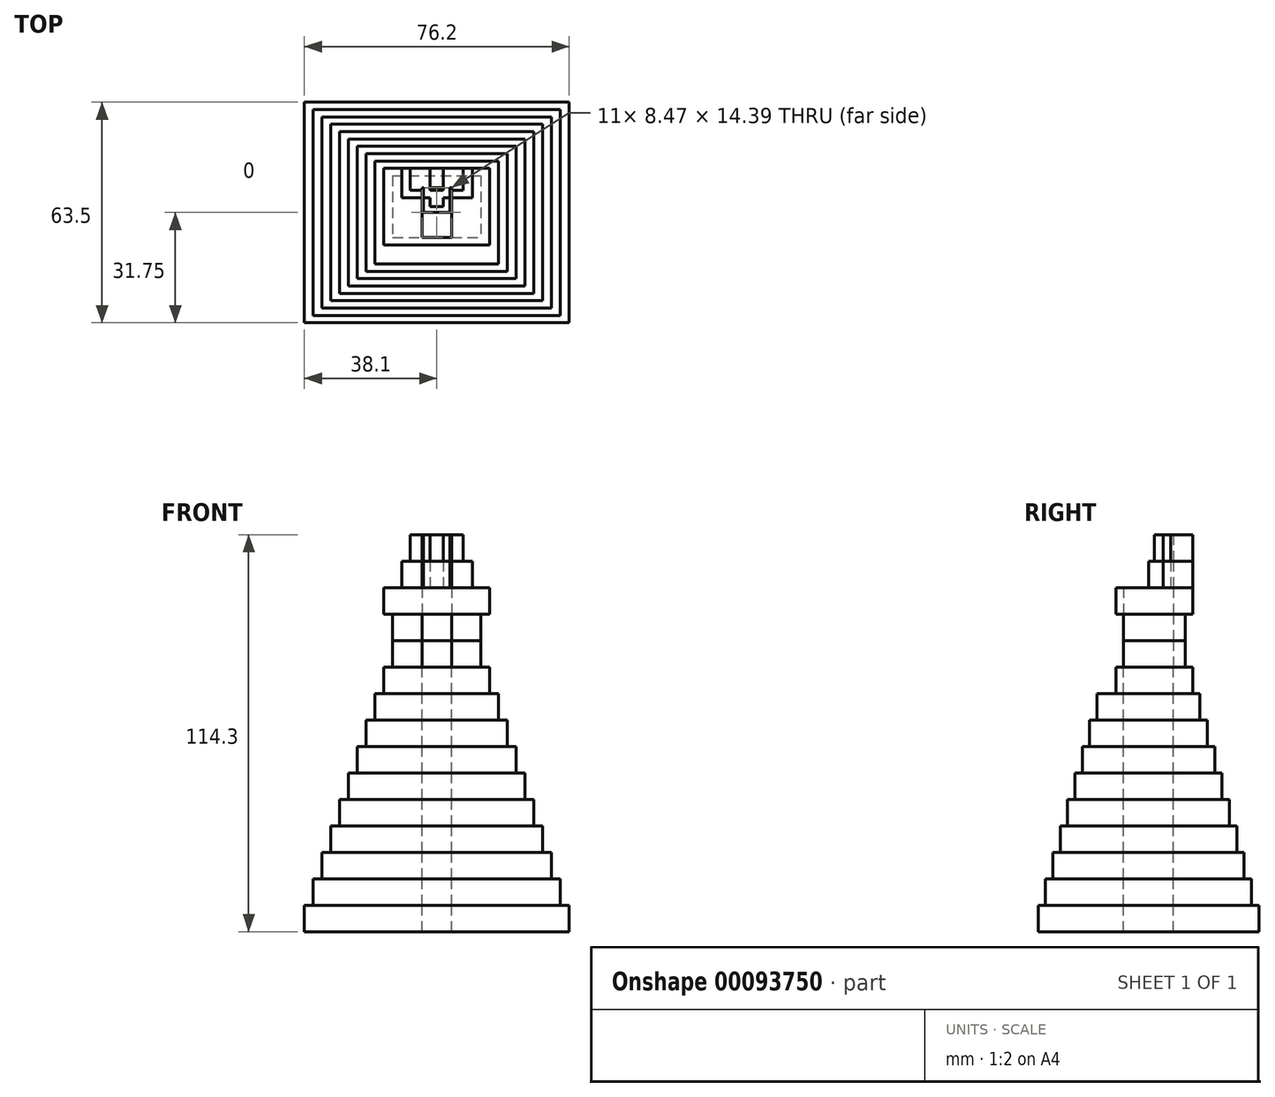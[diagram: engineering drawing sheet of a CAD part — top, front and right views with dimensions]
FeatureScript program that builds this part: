
annotation { "Feature Type Name" : "Feature", "Feature Type Description" : "" }
export const myFeature = defineFeature(function(context is Context, id is Id, definition is map)
    precondition{}
    {
        {
            var Q0;
            Q0=qCreatedBy(makeId("Top.planeOp"),FACE);
            var sketch = newSketch(context, id + "F0", { "sketchPlane" : qUnion([Q0])});
            skLineSegment(sketch, "E0.bottom", {"start": v(-38.1, 31.75) * mm, "end": v(38.1, 31.75) * mm});
            skLineSegment(sketch, "E0.top", {"start": v(-38.1, -31.75) * mm, "end": v(38.1, -31.75) * mm});
            skLineSegment(sketch, "E0.left", {"start": v(-38.1, 31.75) * mm, "end": v(-38.1, -31.75) * mm});
            skLineSegment(sketch, "E0.right", {"start": v(38.1, 31.75) * mm, "end": v(38.1, -31.75) * mm});
            skPoint(sketch, "E0.middle", {"position": v(0, 0) * mm});
            skLineSegment(sketch, "E1.bottom", {"start": v(-35.56, 29.63) * mm, "end": v(35.56, 29.63) * mm});
            skLineSegment(sketch, "E1.top", {"start": v(-35.56, -29.63) * mm, "end": v(35.56, -29.63) * mm});
            skLineSegment(sketch, "E1.left", {"start": v(-35.56, 29.63) * mm, "end": v(-35.56, -29.63) * mm});
            skLineSegment(sketch, "E1.right", {"start": v(35.56, 29.63) * mm, "end": v(35.56, -29.63) * mm});
            skLineSegment(sketch, "E2.bottom", {"start": v(-33.02, 27.52) * mm, "end": v(33.02, 27.52) * mm});
            skLineSegment(sketch, "E2.top", {"start": v(-33.02, -27.52) * mm, "end": v(33.02, -27.52) * mm});
            skLineSegment(sketch, "E2.left", {"start": v(-33.02, 27.52) * mm, "end": v(-33.02, -27.52) * mm});
            skLineSegment(sketch, "E2.right", {"start": v(33.02, 27.52) * mm, "end": v(33.02, -27.52) * mm});
            skLineSegment(sketch, "E3.bottom", {"start": v(-27.94, 23.28) * mm, "end": v(27.94, 23.28) * mm});
            skLineSegment(sketch, "E3.top", {"start": v(-27.94, -23.28) * mm, "end": v(27.94, -23.28) * mm});
            skLineSegment(sketch, "E3.left", {"start": v(-27.94, 23.28) * mm, "end": v(-27.94, -23.28) * mm});
            skLineSegment(sketch, "E3.right", {"start": v(27.94, 23.28) * mm, "end": v(27.94, -23.28) * mm});
            skLineSegment(sketch, "E4.bottom", {"start": v(-30.48, 25.4) * mm, "end": v(30.48, 25.4) * mm});
            skLineSegment(sketch, "E4.top", {"start": v(-30.48, -25.4) * mm, "end": v(30.48, -25.4) * mm});
            skLineSegment(sketch, "E4.left", {"start": v(-30.48, 25.4) * mm, "end": v(-30.48, -25.4) * mm});
            skLineSegment(sketch, "E4.right", {"start": v(30.48, 25.4) * mm, "end": v(30.48, -25.4) * mm});
            skLineSegment(sketch, "E5.bottom", {"start": v(-25.4, 21.17) * mm, "end": v(25.4, 21.17) * mm});
            skLineSegment(sketch, "E5.top", {"start": v(-25.4, -21.17) * mm, "end": v(25.4, -21.17) * mm});
            skLineSegment(sketch, "E5.left", {"start": v(-25.4, 21.17) * mm, "end": v(-25.4, -21.17) * mm});
            skLineSegment(sketch, "E5.right", {"start": v(25.4, 21.17) * mm, "end": v(25.4, -21.17) * mm});
            skLineSegment(sketch, "E6.bottom", {"start": v(-22.86, 19.05) * mm, "end": v(22.86, 19.05) * mm});
            skLineSegment(sketch, "E6.top", {"start": v(-22.86, -19.05) * mm, "end": v(22.86, -19.05) * mm});
            skLineSegment(sketch, "E6.left", {"start": v(-22.86, 19.05) * mm, "end": v(-22.86, -19.05) * mm});
            skLineSegment(sketch, "E6.right", {"start": v(22.86, 19.05) * mm, "end": v(22.86, -19.05) * mm});
            skLineSegment(sketch, "E7.bottom", {"start": v(-20.32, 16.93) * mm, "end": v(20.32, 16.93) * mm});
            skLineSegment(sketch, "E7.top", {"start": v(-20.32, -16.93) * mm, "end": v(20.32, -16.93) * mm});
            skLineSegment(sketch, "E7.left", {"start": v(-20.32, 16.93) * mm, "end": v(-20.32, -16.93) * mm});
            skLineSegment(sketch, "E7.right", {"start": v(20.32, 16.93) * mm, "end": v(20.32, -16.93) * mm});
            skLineSegment(sketch, "E8.bottom", {"start": v(-17.78, 14.82) * mm, "end": v(17.78, 14.82) * mm});
            skLineSegment(sketch, "E8.top", {"start": v(-17.78, -14.82) * mm, "end": v(17.78, -14.82) * mm});
            skLineSegment(sketch, "E8.left", {"start": v(-17.78, 14.82) * mm, "end": v(-17.78, -14.82) * mm});
            skLineSegment(sketch, "E8.right", {"start": v(17.78, 14.82) * mm, "end": v(17.78, -14.82) * mm});
            skLineSegment(sketch, "E9.bottom", {"start": v(-12.7, 10.58) * mm, "end": v(12.7, 10.58) * mm});
            skLineSegment(sketch, "E9.top", {"start": v(-12.7, -7.2) * mm, "end": v(12.7, -7.2) * mm});
            skLineSegment(sketch, "E9.left", {"start": v(-12.7, 10.58) * mm, "end": v(-12.7, -7.2) * mm});
            skLineSegment(sketch, "E9.right", {"start": v(12.7, 10.58) * mm, "end": v(12.7, -7.2) * mm});
            skPoint(sketch, "E9.middle", {"position": v(0, 1.7) * mm});
            skLineSegment(sketch, "E10.bottom", {"start": v(-15.24, 12.7) * mm, "end": v(15.24, 12.7) * mm});
            skLineSegment(sketch, "E10.top", {"start": v(-15.24, -9.31) * mm, "end": v(15.24, -9.31) * mm});
            skLineSegment(sketch, "E10.left", {"start": v(-15.24, 12.7) * mm, "end": v(-15.24, -9.31) * mm});
            skLineSegment(sketch, "E10.right", {"start": v(15.24, 12.7) * mm, "end": v(15.24, -9.31) * mm});
            skLineSegment(sketch, "E11.bottom", {"start": v(-4.23, -7.2) * mm, "end": v(4.23, -7.2) * mm});
            skLineSegment(sketch, "E11.top", {"start": v(-4.23, 7.2) * mm, "end": v(4.23, 7.2) * mm});
            skLineSegment(sketch, "E11.left", {"start": v(-4.23, -7.2) * mm, "end": v(-4.23, 7.2) * mm});
            skLineSegment(sketch, "E11.right", {"start": v(4.23, -7.2) * mm, "end": v(4.23, 7.2) * mm});
            skSolve(sketch);
        }
        {
            var Q0;
            Q0=makeQuery(id+"F0.imprint","IMPRINT",FACE,{"disambiguationData":[TD([[makeQuery(id+"F0.imprint","IMPRINT",EDGE,{"derivedFrom":sQuery(id+"F0.wireOp",EDGE,"E0.bottom")}),-1.0]])]});
            var Q1;
            Q1=makeQuery(id+"F0.imprint","IMPRINT",FACE,{"disambiguationData":[TD([[makeQuery(id+"F0.imprint","IMPRINT",EDGE,{"derivedFrom":sQuery(id+"F0.wireOp",EDGE,"E3.bottom")}),-1.0]])]});
            var Q2;
            Q2=makeQuery(id+"F0.imprint","IMPRINT",FACE,{"disambiguationData":[TD([[makeQuery(id+"F0.imprint","IMPRINT",EDGE,{"derivedFrom":sQuery(id+"F0.wireOp",EDGE,"E2.bottom")}),-1.0]])]});
            var Q3;
            Q3=makeQuery(id+"F0.imprint","IMPRINT",FACE,{"disambiguationData":[TD([[makeQuery(id+"F0.imprint","IMPRINT",EDGE,{"derivedFrom":sQuery(id+"F0.wireOp",EDGE,"E1.bottom")}),-1.0]])]});
            var Q4;
            Q4=makeQuery(id+"F0.imprint","IMPRINT",FACE,{"disambiguationData":[TD([[makeQuery(id+"F0.imprint","IMPRINT",EDGE,{"derivedFrom":sQuery(id+"F0.wireOp",EDGE,"E3.bottom")}),1.0]])]});
            var Q5;
            Q5=makeQuery(id+"F0.imprint","IMPRINT",FACE,{"disambiguationData":[TD([[makeQuery(id+"F0.imprint","IMPRINT",EDGE,{"derivedFrom":sQuery(id+"F0.wireOp",EDGE,"E6.bottom")}),-1.0]])]});
            var Q6;
            Q6=makeQuery(id+"F0.imprint","IMPRINT",FACE,{"disambiguationData":[TD([[makeQuery(id+"F0.imprint","IMPRINT",EDGE,{"derivedFrom":sQuery(id+"F0.wireOp",EDGE,"E5.bottom")}),-1.0]])]});
            var Q7;
            Q7=makeQuery(id+"F0.imprint","IMPRINT",FACE,{"disambiguationData":[TD([[makeQuery(id+"F0.imprint","IMPRINT",EDGE,{"derivedFrom":sQuery(id+"F0.wireOp",EDGE,"E7.bottom")}),-1.0]])]});
            var Q8;
            Q8=makeQuery(id+"F0.imprint","IMPRINT",FACE,{"disambiguationData":[TD([[makeQuery(id+"F0.imprint","IMPRINT",EDGE,{"derivedFrom":sQuery(id+"F0.wireOp",EDGE,"E8.bottom")}),-1.0]])]});
            var Q9;
            Q9=makeQuery(id+"F0.imprint","IMPRINT",FACE,{"disambiguationData":[TD([[makeQuery(id+"F0.imprint","IMPRINT",EDGE,{"derivedFrom":sQuery(id+"F0.wireOp",EDGE,"E9.bottom")}),1.0]])]});
            var Q10;
            Q10=makeQuery(id+"F0.imprint","IMPRINT",FACE,{"disambiguationData":[TD([[makeQuery(id+"F0.imprint","IMPRINT",EDGE,{"derivedFrom":sQuery(id+"F0.wireOp",EDGE,"E9.bottom")}),-1.0]])]});
            var Q11;
            Q11=makeQuery(id+"F0.imprint","IMPRINT",FACE,{"disambiguationData":[TD([[makeQuery(id+"F0.imprint","IMPRINT",EDGE,{"derivedFrom":sQuery(id+"F0.wireOp",EDGE,"E11.bottom")}),1.0]])]});
            extrude(context, id + "F1", {"entities" : qUnion([Q0, Q1, Q2, Q3, Q4, Q5, Q6, Q7, Q8, Q9, Q10, Q11]), "oppositeDirection" : true, "depth" : 76.2 * mm, "hasSecondDirection" : true, "secondDirectionOppositeDirection" : true, "secondDirectionDepth" : 68.58 * mm});
        }
        {
            var Q0;
            Q0=makeQuery(id+"F0.imprint","IMPRINT",FACE,{"disambiguationData":[TD([[makeQuery(id+"F0.imprint","IMPRINT",EDGE,{"derivedFrom":sQuery(id+"F0.wireOp",EDGE,"E1.bottom")}),-1.0]])]});
            var Q1;
            Q1=makeQuery(id+"F0.imprint","IMPRINT",FACE,{"disambiguationData":[TD([[makeQuery(id+"F0.imprint","IMPRINT",EDGE,{"derivedFrom":sQuery(id+"F0.wireOp",EDGE,"E5.bottom")}),-1.0]])]});
            var Q2;
            Q2=makeQuery(id+"F0.imprint","IMPRINT",FACE,{"disambiguationData":[TD([[makeQuery(id+"F0.imprint","IMPRINT",EDGE,{"derivedFrom":sQuery(id+"F0.wireOp",EDGE,"E3.bottom")}),-1.0]])]});
            var Q3;
            Q3=makeQuery(id+"F0.imprint","IMPRINT",FACE,{"disambiguationData":[TD([[makeQuery(id+"F0.imprint","IMPRINT",EDGE,{"derivedFrom":sQuery(id+"F0.wireOp",EDGE,"E2.bottom")}),-1.0]])]});
            var Q4;
            Q4=makeQuery(id+"F0.imprint","IMPRINT",FACE,{"disambiguationData":[TD([[makeQuery(id+"F0.imprint","IMPRINT",EDGE,{"derivedFrom":sQuery(id+"F0.wireOp",EDGE,"E3.bottom")}),1.0]])]});
            var Q5;
            Q5=makeQuery(id+"F0.imprint","IMPRINT",FACE,{"disambiguationData":[TD([[makeQuery(id+"F0.imprint","IMPRINT",EDGE,{"derivedFrom":sQuery(id+"F0.wireOp",EDGE,"E8.bottom")}),-1.0]])]});
            var Q6;
            Q6=makeQuery(id+"F0.imprint","IMPRINT",FACE,{"disambiguationData":[TD([[makeQuery(id+"F0.imprint","IMPRINT",EDGE,{"derivedFrom":sQuery(id+"F0.wireOp",EDGE,"E7.bottom")}),-1.0]])]});
            var Q7;
            Q7=makeQuery(id+"F0.imprint","IMPRINT",FACE,{"disambiguationData":[TD([[makeQuery(id+"F0.imprint","IMPRINT",EDGE,{"derivedFrom":sQuery(id+"F0.wireOp",EDGE,"E6.bottom")}),-1.0]])]});
            var Q8;
            Q8=makeQuery(id+"F0.imprint","IMPRINT",FACE,{"disambiguationData":[TD([[makeQuery(id+"F0.imprint","IMPRINT",EDGE,{"derivedFrom":sQuery(id+"F0.wireOp",EDGE,"E9.bottom")}),-1.0]])]});
            var Q9;
            Q9=makeQuery(id+"F0.imprint","IMPRINT",FACE,{"disambiguationData":[TD([[makeQuery(id+"F0.imprint","IMPRINT",EDGE,{"derivedFrom":sQuery(id+"F0.wireOp",EDGE,"E9.bottom")}),1.0]])]});
            var Q10;
            Q10=makeQuery(id+"F0.imprint","IMPRINT",FACE,{"disambiguationData":[TD([[makeQuery(id+"F0.imprint","IMPRINT",EDGE,{"derivedFrom":sQuery(id+"F0.wireOp",EDGE,"E11.bottom")}),1.0]])]});
            extrude(context, id + "F2", {"entities" : qUnion([Q0, Q1, Q2, Q3, Q4, Q5, Q6, Q7, Q8, Q9, Q10]), "oppositeDirection" : true, "depth" : 68.58 * mm, "hasSecondDirection" : true, "secondDirectionOppositeDirection" : true, "secondDirectionDepth" : 60.96 * mm});
        }
        {
            var Q0;
            Q0=makeQuery(id+"F0.imprint","IMPRINT",FACE,{"disambiguationData":[TD([[makeQuery(id+"F0.imprint","IMPRINT",EDGE,{"derivedFrom":sQuery(id+"F0.wireOp",EDGE,"E2.bottom")}),-1.0]])]});
            var Q1;
            Q1=makeQuery(id+"F0.imprint","IMPRINT",FACE,{"disambiguationData":[TD([[makeQuery(id+"F0.imprint","IMPRINT",EDGE,{"derivedFrom":sQuery(id+"F0.wireOp",EDGE,"E3.bottom")}),1.0]])]});
            var Q2;
            Q2=makeQuery(id+"F0.imprint","IMPRINT",FACE,{"disambiguationData":[TD([[makeQuery(id+"F0.imprint","IMPRINT",EDGE,{"derivedFrom":sQuery(id+"F0.wireOp",EDGE,"E5.bottom")}),-1.0]])]});
            var Q3;
            Q3=makeQuery(id+"F0.imprint","IMPRINT",FACE,{"disambiguationData":[TD([[makeQuery(id+"F0.imprint","IMPRINT",EDGE,{"derivedFrom":sQuery(id+"F0.wireOp",EDGE,"E3.bottom")}),-1.0]])]});
            var Q4;
            Q4=makeQuery(id+"F0.imprint","IMPRINT",FACE,{"disambiguationData":[TD([[makeQuery(id+"F0.imprint","IMPRINT",EDGE,{"derivedFrom":sQuery(id+"F0.wireOp",EDGE,"E6.bottom")}),-1.0]])]});
            var Q5;
            Q5=makeQuery(id+"F0.imprint","IMPRINT",FACE,{"disambiguationData":[TD([[makeQuery(id+"F0.imprint","IMPRINT",EDGE,{"derivedFrom":sQuery(id+"F0.wireOp",EDGE,"E8.bottom")}),-1.0]])]});
            var Q6;
            Q6=makeQuery(id+"F0.imprint","IMPRINT",FACE,{"disambiguationData":[TD([[makeQuery(id+"F0.imprint","IMPRINT",EDGE,{"derivedFrom":sQuery(id+"F0.wireOp",EDGE,"E9.bottom")}),1.0]])]});
            var Q7;
            Q7=makeQuery(id+"F0.imprint","IMPRINT",FACE,{"disambiguationData":[TD([[makeQuery(id+"F0.imprint","IMPRINT",EDGE,{"derivedFrom":sQuery(id+"F0.wireOp",EDGE,"E9.bottom")}),-1.0]])]});
            var Q8;
            Q8=makeQuery(id+"F0.imprint","IMPRINT",FACE,{"disambiguationData":[TD([[makeQuery(id+"F0.imprint","IMPRINT",EDGE,{"derivedFrom":sQuery(id+"F0.wireOp",EDGE,"E11.bottom")}),1.0]])]});
            var Q9;
            Q9=makeQuery(id+"F0.imprint","IMPRINT",FACE,{"disambiguationData":[TD([[makeQuery(id+"F0.imprint","IMPRINT",EDGE,{"derivedFrom":sQuery(id+"F0.wireOp",EDGE,"E7.bottom")}),-1.0]])]});
            extrude(context, id + "F3", {"entities" : qUnion([Q0, Q1, Q2, Q3, Q4, Q5, Q6, Q7, Q8, Q9]), "oppositeDirection" : true, "depth" : 60.96 * mm, "hasSecondDirection" : true, "secondDirectionOppositeDirection" : true, "secondDirectionDepth" : 53.34 * mm});
        }
        {
            var Q0;
            Q0=makeQuery(id+"F0.imprint","IMPRINT",FACE,{"disambiguationData":[TD([[makeQuery(id+"F0.imprint","IMPRINT",EDGE,{"derivedFrom":sQuery(id+"F0.wireOp",EDGE,"E3.bottom")}),1.0]])]});
            var Q1;
            Q1=makeQuery(id+"F0.imprint","IMPRINT",FACE,{"disambiguationData":[TD([[makeQuery(id+"F0.imprint","IMPRINT",EDGE,{"derivedFrom":sQuery(id+"F0.wireOp",EDGE,"E3.bottom")}),-1.0]])]});
            var Q2;
            Q2=makeQuery(id+"F0.imprint","IMPRINT",FACE,{"disambiguationData":[TD([[makeQuery(id+"F0.imprint","IMPRINT",EDGE,{"derivedFrom":sQuery(id+"F0.wireOp",EDGE,"E5.bottom")}),-1.0]])]});
            var Q3;
            Q3=makeQuery(id+"F0.imprint","IMPRINT",FACE,{"disambiguationData":[TD([[makeQuery(id+"F0.imprint","IMPRINT",EDGE,{"derivedFrom":sQuery(id+"F0.wireOp",EDGE,"E6.bottom")}),-1.0]])]});
            var Q4;
            Q4=makeQuery(id+"F0.imprint","IMPRINT",FACE,{"disambiguationData":[TD([[makeQuery(id+"F0.imprint","IMPRINT",EDGE,{"derivedFrom":sQuery(id+"F0.wireOp",EDGE,"E8.bottom")}),-1.0]])]});
            var Q5;
            Q5=makeQuery(id+"F0.imprint","IMPRINT",FACE,{"disambiguationData":[TD([[makeQuery(id+"F0.imprint","IMPRINT",EDGE,{"derivedFrom":sQuery(id+"F0.wireOp",EDGE,"E7.bottom")}),-1.0]])]});
            var Q6;
            Q6=makeQuery(id+"F0.imprint","IMPRINT",FACE,{"disambiguationData":[TD([[makeQuery(id+"F0.imprint","IMPRINT",EDGE,{"derivedFrom":sQuery(id+"F0.wireOp",EDGE,"E9.bottom")}),1.0]])]});
            var Q7;
            Q7=makeQuery(id+"F0.imprint","IMPRINT",FACE,{"disambiguationData":[TD([[makeQuery(id+"F0.imprint","IMPRINT",EDGE,{"derivedFrom":sQuery(id+"F0.wireOp",EDGE,"E9.bottom")}),-1.0]])]});
            var Q8;
            Q8=makeQuery(id+"F0.imprint","IMPRINT",FACE,{"disambiguationData":[TD([[makeQuery(id+"F0.imprint","IMPRINT",EDGE,{"derivedFrom":sQuery(id+"F0.wireOp",EDGE,"E11.bottom")}),1.0]])]});
            extrude(context, id + "F4", {"entities" : qUnion([Q0, Q1, Q2, Q3, Q4, Q5, Q6, Q7, Q8]), "oppositeDirection" : true, "depth" : 53.34 * mm, "hasSecondDirection" : true, "secondDirectionOppositeDirection" : true, "secondDirectionDepth" : 45.72 * mm});
        }
        {
            var Q0;
            Q0=makeQuery(id+"F0.imprint","IMPRINT",FACE,{"disambiguationData":[TD([[makeQuery(id+"F0.imprint","IMPRINT",EDGE,{"derivedFrom":sQuery(id+"F0.wireOp",EDGE,"E3.bottom")}),-1.0]])]});
            var Q1;
            Q1=makeQuery(id+"F0.imprint","IMPRINT",FACE,{"disambiguationData":[TD([[makeQuery(id+"F0.imprint","IMPRINT",EDGE,{"derivedFrom":sQuery(id+"F0.wireOp",EDGE,"E5.bottom")}),-1.0]])]});
            var Q2;
            Q2=makeQuery(id+"F0.imprint","IMPRINT",FACE,{"disambiguationData":[TD([[makeQuery(id+"F0.imprint","IMPRINT",EDGE,{"derivedFrom":sQuery(id+"F0.wireOp",EDGE,"E6.bottom")}),-1.0]])]});
            var Q3;
            Q3=makeQuery(id+"F0.imprint","IMPRINT",FACE,{"disambiguationData":[TD([[makeQuery(id+"F0.imprint","IMPRINT",EDGE,{"derivedFrom":sQuery(id+"F0.wireOp",EDGE,"E7.bottom")}),-1.0]])]});
            var Q4;
            Q4=makeQuery(id+"F0.imprint","IMPRINT",FACE,{"disambiguationData":[TD([[makeQuery(id+"F0.imprint","IMPRINT",EDGE,{"derivedFrom":sQuery(id+"F0.wireOp",EDGE,"E8.bottom")}),-1.0]])]});
            var Q5;
            Q5=makeQuery(id+"F0.imprint","IMPRINT",FACE,{"disambiguationData":[TD([[makeQuery(id+"F0.imprint","IMPRINT",EDGE,{"derivedFrom":sQuery(id+"F0.wireOp",EDGE,"E9.bottom")}),1.0]])]});
            var Q6;
            Q6=makeQuery(id+"F0.imprint","IMPRINT",FACE,{"disambiguationData":[TD([[makeQuery(id+"F0.imprint","IMPRINT",EDGE,{"derivedFrom":sQuery(id+"F0.wireOp",EDGE,"E11.bottom")}),1.0]])]});
            var Q7;
            Q7=makeQuery(id+"F0.imprint","IMPRINT",FACE,{"disambiguationData":[TD([[makeQuery(id+"F0.imprint","IMPRINT",EDGE,{"derivedFrom":sQuery(id+"F0.wireOp",EDGE,"E9.bottom")}),-1.0]])]});
            extrude(context, id + "F5", {"entities" : qUnion([Q0, Q1, Q2, Q3, Q4, Q5, Q6, Q7]), "oppositeDirection" : true, "depth" : 45.72 * mm, "hasSecondDirection" : true, "secondDirectionOppositeDirection" : true, "secondDirectionDepth" : 38.1 * mm});
        }
        {
            var Q0;
            Q0=makeQuery(id+"F0.imprint","IMPRINT",FACE,{"disambiguationData":[TD([[makeQuery(id+"F0.imprint","IMPRINT",EDGE,{"derivedFrom":sQuery(id+"F0.wireOp",EDGE,"E5.bottom")}),-1.0]])]});
            var Q1;
            Q1=makeQuery(id+"F0.imprint","IMPRINT",FACE,{"disambiguationData":[TD([[makeQuery(id+"F0.imprint","IMPRINT",EDGE,{"derivedFrom":sQuery(id+"F0.wireOp",EDGE,"E7.bottom")}),-1.0]])]});
            var Q2;
            Q2=makeQuery(id+"F0.imprint","IMPRINT",FACE,{"disambiguationData":[TD([[makeQuery(id+"F0.imprint","IMPRINT",EDGE,{"derivedFrom":sQuery(id+"F0.wireOp",EDGE,"E8.bottom")}),-1.0]])]});
            var Q3;
            Q3=makeQuery(id+"F0.imprint","IMPRINT",FACE,{"disambiguationData":[TD([[makeQuery(id+"F0.imprint","IMPRINT",EDGE,{"derivedFrom":sQuery(id+"F0.wireOp",EDGE,"E9.bottom")}),-1.0]])]});
            var Q4;
            Q4=makeQuery(id+"F0.imprint","IMPRINT",FACE,{"disambiguationData":[TD([[makeQuery(id+"F0.imprint","IMPRINT",EDGE,{"derivedFrom":sQuery(id+"F0.wireOp",EDGE,"E11.bottom")}),1.0]])]});
            var Q5;
            Q5=makeQuery(id+"F0.imprint","IMPRINT",FACE,{"disambiguationData":[TD([[makeQuery(id+"F0.imprint","IMPRINT",EDGE,{"derivedFrom":sQuery(id+"F0.wireOp",EDGE,"E9.bottom")}),1.0]])]});
            var Q6;
            Q6=makeQuery(id+"F0.imprint","IMPRINT",FACE,{"disambiguationData":[TD([[makeQuery(id+"F0.imprint","IMPRINT",EDGE,{"derivedFrom":sQuery(id+"F0.wireOp",EDGE,"E6.bottom")}),-1.0]])]});
            extrude(context, id + "F6", {"entities" : qUnion([Q0, Q1, Q2, Q3, Q4, Q5, Q6]), "oppositeDirection" : true, "depth" : 38.1 * mm, "hasSecondDirection" : true, "secondDirectionOppositeDirection" : true, "secondDirectionDepth" : 30.48 * mm});
        }
        {
            var Q0;
            Q0=makeQuery(id+"F0.imprint","IMPRINT",FACE,{"disambiguationData":[TD([[makeQuery(id+"F0.imprint","IMPRINT",EDGE,{"derivedFrom":sQuery(id+"F0.wireOp",EDGE,"E6.bottom")}),-1.0]])]});
            var Q1;
            Q1=makeQuery(id+"F0.imprint","IMPRINT",FACE,{"disambiguationData":[TD([[makeQuery(id+"F0.imprint","IMPRINT",EDGE,{"derivedFrom":sQuery(id+"F0.wireOp",EDGE,"E7.bottom")}),-1.0]])]});
            var Q2;
            Q2=makeQuery(id+"F0.imprint","IMPRINT",FACE,{"disambiguationData":[TD([[makeQuery(id+"F0.imprint","IMPRINT",EDGE,{"derivedFrom":sQuery(id+"F0.wireOp",EDGE,"E8.bottom")}),-1.0]])]});
            var Q3;
            Q3=makeQuery(id+"F0.imprint","IMPRINT",FACE,{"disambiguationData":[TD([[makeQuery(id+"F0.imprint","IMPRINT",EDGE,{"derivedFrom":sQuery(id+"F0.wireOp",EDGE,"E9.bottom")}),1.0]])]});
            var Q4;
            Q4=makeQuery(id+"F0.imprint","IMPRINT",FACE,{"disambiguationData":[TD([[makeQuery(id+"F0.imprint","IMPRINT",EDGE,{"derivedFrom":sQuery(id+"F0.wireOp",EDGE,"E9.bottom")}),-1.0]])]});
            var Q5;
            Q5=makeQuery(id+"F0.imprint","IMPRINT",FACE,{"disambiguationData":[TD([[makeQuery(id+"F0.imprint","IMPRINT",EDGE,{"derivedFrom":sQuery(id+"F0.wireOp",EDGE,"E11.bottom")}),1.0]])]});
            extrude(context, id + "F7", {"entities" : qUnion([Q0, Q1, Q2, Q3, Q4, Q5]), "oppositeDirection" : true, "depth" : 30.48 * mm, "hasSecondDirection" : true, "secondDirectionOppositeDirection" : true, "secondDirectionDepth" : 22.86 * mm});
        }
        {
            var Q0;
            Q0=makeQuery(id+"F0.imprint","IMPRINT",FACE,{"disambiguationData":[TD([[makeQuery(id+"F0.imprint","IMPRINT",EDGE,{"derivedFrom":sQuery(id+"F0.wireOp",EDGE,"E7.bottom")}),-1.0]])]});
            var Q1;
            Q1=makeQuery(id+"F0.imprint","IMPRINT",FACE,{"disambiguationData":[TD([[makeQuery(id+"F0.imprint","IMPRINT",EDGE,{"derivedFrom":sQuery(id+"F0.wireOp",EDGE,"E8.bottom")}),-1.0]])]});
            var Q2;
            Q2=makeQuery(id+"F0.imprint","IMPRINT",FACE,{"disambiguationData":[TD([[makeQuery(id+"F0.imprint","IMPRINT",EDGE,{"derivedFrom":sQuery(id+"F0.wireOp",EDGE,"E9.bottom")}),1.0]])]});
            var Q3;
            Q3=makeQuery(id+"F0.imprint","IMPRINT",FACE,{"disambiguationData":[TD([[makeQuery(id+"F0.imprint","IMPRINT",EDGE,{"derivedFrom":sQuery(id+"F0.wireOp",EDGE,"E9.bottom")}),-1.0]])]});
            var Q4;
            Q4=makeQuery(id+"F0.imprint","IMPRINT",FACE,{"disambiguationData":[TD([[makeQuery(id+"F0.imprint","IMPRINT",EDGE,{"derivedFrom":sQuery(id+"F0.wireOp",EDGE,"E11.bottom")}),1.0]])]});
            extrude(context, id + "F8", {"entities" : qUnion([Q0, Q1, Q2, Q3, Q4]), "oppositeDirection" : true, "depth" : 22.86 * mm, "hasSecondDirection" : true, "secondDirectionOppositeDirection" : true, "secondDirectionDepth" : 15.24 * mm});
        }
        {
            var Q0;
            Q0=makeQuery(id+"F0.imprint","IMPRINT",FACE,{"disambiguationData":[TD([[makeQuery(id+"F0.imprint","IMPRINT",EDGE,{"derivedFrom":sQuery(id+"F0.wireOp",EDGE,"E8.bottom")}),-1.0]])]});
            var Q1;
            Q1=makeQuery(id+"F0.imprint","IMPRINT",FACE,{"disambiguationData":[TD([[makeQuery(id+"F0.imprint","IMPRINT",EDGE,{"derivedFrom":sQuery(id+"F0.wireOp",EDGE,"LNLqUZsx-ek0y-c9DL-dkz8-nugYkIzDSpda.bottom")}),-1.0]])]});
            var Q2;
            Q2=makeQuery(id+"F0.imprint","IMPRINT",FACE,{"disambiguationData":[TD([[makeQuery(id+"F0.imprint","IMPRINT",EDGE,{"derivedFrom":sQuery(id+"F0.wireOp",EDGE,"E9.bottom")}),-1.0]])]});
            var Q3;
            Q3=makeQuery(id+"F0.imprint","IMPRINT",FACE,{"disambiguationData":[TD([[makeQuery(id+"F0.imprint","IMPRINT",EDGE,{"derivedFrom":sQuery(id+"F0.wireOp",EDGE,"E9.bottom")}),1.0]])]});
            var Q4;
            Q4=makeQuery(id+"F0.imprint","IMPRINT",FACE,{"disambiguationData":[TD([[makeQuery(id+"F0.imprint","IMPRINT",EDGE,{"derivedFrom":sQuery(id+"F0.wireOp",EDGE,"E11.bottom")}),1.0]])]});
            extrude(context, id + "F9", {"entities" : qUnion([Q0, Q1, Q2, Q3, Q4]), "oppositeDirection" : true, "depth" : 15.24 * mm, "hasSecondDirection" : true, "secondDirectionOppositeDirection" : true, "secondDirectionDepth" : 7.62 * mm});
        }
        {
            var Q0;
            Q0=makeQuery(id+"F0.imprint","IMPRINT",FACE,{"disambiguationData":[TD([[makeQuery(id+"F0.imprint","IMPRINT",EDGE,{"derivedFrom":sQuery(id+"F0.wireOp",EDGE,"E9.bottom")}),1.0]])]});
            var Q1;
            Q1=makeQuery(id+"F0.imprint","IMPRINT",FACE,{"disambiguationData":[TD([[makeQuery(id+"F0.imprint","IMPRINT",EDGE,{"derivedFrom":sQuery(id+"F0.wireOp",EDGE,"E9.bottom")}),-1.0]])]});
            var Q2;
            Q2=makeQuery(id+"F0.imprint","IMPRINT",FACE,{"disambiguationData":[TD([[makeQuery(id+"F0.imprint","IMPRINT",EDGE,{"derivedFrom":sQuery(id+"F0.wireOp",EDGE,"E11.bottom")}),1.0]])]});
            extrude(context, id + "F10", {"entities" : qUnion([Q0, Q1, Q2]), "oppositeDirection" : true, "depth" : 7.62 * mm});
        }
        {
            var Q0;
            Q0=makeQuery(id+"F0.imprint","IMPRINT",FACE,{"disambiguationData":[TD([[makeQuery(id+"F0.imprint","IMPRINT",EDGE,{"derivedFrom":sQuery(id+"F0.wireOp",EDGE,"E9.bottom")}),-1.0]])]});
            extrude(context, id + "F11", {"entities" : qUnion([Q0]), "depth" : 7.62 * mm});
        }
        {
            var Q0;
            Q0=makeQuery(id+"F0.imprint","IMPRINT",FACE,{"disambiguationData":[TD([[makeQuery(id+"F0.imprint","IMPRINT",EDGE,{"derivedFrom":sQuery(id+"F0.wireOp",EDGE,"E9.bottom")}),1.0]])]});
            var Q1;
            Q1=makeQuery(id+"F0.imprint","IMPRINT",FACE,{"disambiguationData":[TD([[makeQuery(id+"F0.imprint","IMPRINT",EDGE,{"derivedFrom":sQuery(id+"F0.wireOp",EDGE,"E9.bottom")}),-1.0]])]});
            var Q2;
            Q2=makeQuery(id+"F0.imprint","IMPRINT",FACE,{"disambiguationData":[TD([[makeQuery(id+"F0.imprint","IMPRINT",EDGE,{"derivedFrom":sQuery(id+"F0.wireOp",EDGE,"E11.bottom")}),1.0]])]});
            extrude(context, id + "F12", {"entities" : qUnion([Q0, Q1, Q2]), "operationType" : NewBodyOperationType.ADD, "depth" : 22.86 * mm, "hasSecondDirection" : true, "secondDirectionOppositeDirection" : false, "secondDirectionDepth" : 15.24 * mm});
        }
        {
            var Q0;
            Q0=makeQuery(id+"F12.opExtrude","CAP_FACE",FACE,{"disambiguationData":[OSD([sQuery(id+"F0.wireOp",EDGE,"E10.bottom"),sQuery(id+"F0.wireOp",EDGE,"E10.top"),sQuery(id+"F0.wireOp",EDGE,"E10.left"),sQuery(id+"F0.wireOp",EDGE,"E10.right")])],"isStart":false});
            var sketch = newSketch(context, id + "F13", { "sketchPlane" : qUnion([Q0])});
            skLineSegment(sketch, "E12.bottom", {"start": v(-10.13, 12.7) * mm, "end": v(10.2, 12.7) * mm});
            skLineSegment(sketch, "E12.top", {"start": v(-10.13, 4.23) * mm, "end": v(10.2, 4.23) * mm});
            skLineSegment(sketch, "E12.left", {"start": v(-10.13, 12.7) * mm, "end": v(-10.13, 4.23) * mm});
            skLineSegment(sketch, "E12.right", {"start": v(10.2, 12.7) * mm, "end": v(10.2, 4.23) * mm});
            skLineSegment(sketch, "E13", {"start": v(10.2, 12.7) * mm, "end": v(-10.13, 12.7) * mm});
            skPoint(sketch, "E14", {"position": v(0, 12.7) * mm});
            skLineSegment(sketch, "E15.bottom", {"start": v(-3.8, 12.7) * mm, "end": v(3.81, 12.7) * mm});
            skLineSegment(sketch, "E15.top", {"start": v(-3.8, 0) * mm, "end": v(3.81, 0) * mm});
            skLineSegment(sketch, "E15.left", {"start": v(-3.8, 12.7) * mm, "end": v(-3.8, 0) * mm});
            skLineSegment(sketch, "E15.right", {"start": v(3.81, 12.7) * mm, "end": v(3.81, 0) * mm});
            skLineSegment(sketch, "E16.bottom", {"start": v(-7.62, 12.7) * mm, "end": v(7.62, 12.7) * mm});
            skLineSegment(sketch, "E16.top", {"start": v(-7.62, 6.35) * mm, "end": v(7.62, 6.35) * mm});
            skLineSegment(sketch, "E16.left", {"start": v(-7.62, 12.7) * mm, "end": v(-7.62, 6.35) * mm});
            skLineSegment(sketch, "E16.right", {"start": v(7.62, 12.7) * mm, "end": v(7.62, 6.35) * mm});
            skLineSegment(sketch, "E17.bottom", {"start": v(-1.9, 12.7) * mm, "end": v(1.9, 12.7) * mm});
            skLineSegment(sketch, "E17.top", {"start": v(-1.9, 1.7) * mm, "end": v(1.9, 1.7) * mm});
            skLineSegment(sketch, "E17.left", {"start": v(-1.9, 12.7) * mm, "end": v(-1.9, 1.7) * mm});
            skLineSegment(sketch, "E17.right", {"start": v(1.9, 12.7) * mm, "end": v(1.9, 1.7) * mm});
            skSolve(sketch);
        }
        {
            var Q0;
            {var subQ1=sQuery(id+"F13.wireOp",EDGE,"E12.left");Q0=makeQuery(id+"F13.imprint","IMPRINT",FACE,{"disambiguationData":[TD([[makeQuery(id+"F13.imprint","IMPRINT",EDGE,{"derivedFrom":subQ1}),1.0]])]});}
            var Q1;
            {var subQ0=sQuery(id+"F13.wireOp",EDGE,"E17.right");var subQ1=sQuery(id+"F13.wireOp",EDGE,"E12.top");var subQ2=makeQuery(id+"F13.imprint","INTERSECT",VERTEX,{"derivedFrom":[subQ1,subQ0]});Q1=makeQuery(id+"F13.imprint","IMPRINT",FACE,{"disambiguationData":[TD([[makeQuery(id+"F13.imprint","IMPRINT",EDGE,{"disambiguationData":[TD([[subQ2,-1.0]])],"derivedFrom":subQ1}),1.0]])]});}
            var Q2;
            {var subQ0=sQuery(id+"F13.wireOp",EDGE,"E15.left");var subQ1=sQuery(id+"F13.wireOp",EDGE,"E12.top");var subQ2=makeQuery(id+"F13.imprint","INTERSECT",VERTEX,{"derivedFrom":[subQ1,subQ0]});Q2=makeQuery(id+"F13.imprint","IMPRINT",FACE,{"disambiguationData":[TD([[makeQuery(id+"F13.imprint","IMPRINT",EDGE,{"disambiguationData":[TD([[subQ2,-1.0]])],"derivedFrom":subQ1}),1.0]])]});}
            var Q3;
            {var subQ1=sQuery(id+"F13.wireOp",EDGE,"E15.top");Q3=makeQuery(id+"F13.imprint","IMPRINT",FACE,{"disambiguationData":[TD([[makeQuery(id+"F13.imprint","IMPRINT",EDGE,{"derivedFrom":subQ1}),1.0]])]});}
            var Q4;
            {var subQ1=sQuery(id+"F13.wireOp",EDGE,"E12.right");Q4=makeQuery(id+"F13.imprint","IMPRINT",FACE,{"disambiguationData":[TD([[makeQuery(id+"F13.imprint","IMPRINT",EDGE,{"derivedFrom":subQ1}),-1.0]])]});}
            var Q5;
            {var subQ5=sQuery(id+"F13.wireOp",EDGE,"E16.right");Q5=makeQuery(id+"F13.imprint","IMPRINT",FACE,{"disambiguationData":[TD([[makeQuery(id+"F13.imprint","IMPRINT",EDGE,{"derivedFrom":subQ5}),-1.0]])]});}
            var Q6;
            {var subQ0=sQuery(id+"F13.wireOp",EDGE,"E16.bottom");var subQ1=sQuery(id+"F13.wireOp",EDGE,"E15.right");var subQ2=makeQuery(id+"F13.imprint","INTERSECT",VERTEX,{"derivedFrom":[subQ1,subQ0]});Q6=makeQuery(id+"F13.imprint","IMPRINT",FACE,{"disambiguationData":[TD([[makeQuery(id+"F13.imprint","IMPRINT",EDGE,{"disambiguationData":[TD([[subQ2,-1.0]])],"derivedFrom":subQ1}),-1.0]])]});}
            var Q7;
            {var subQ5=sQuery(id+"F13.wireOp",EDGE,"E17.bottom");Q7=makeQuery(id+"F13.imprint","IMPRINT",FACE,{"disambiguationData":[TD([[makeQuery(id+"F13.imprint","IMPRINT",EDGE,{"derivedFrom":subQ5}),-1.0]])]});}
            var Q8;
            {var subQ0=sQuery(id+"F13.wireOp",EDGE,"E17.left");var subQ1=sQuery(id+"F13.wireOp",EDGE,"E12.top");var subQ2=makeQuery(id+"F13.imprint","INTERSECT",VERTEX,{"derivedFrom":[subQ1,subQ0]});Q8=makeQuery(id+"F13.imprint","IMPRINT",FACE,{"disambiguationData":[TD([[makeQuery(id+"F13.imprint","IMPRINT",EDGE,{"disambiguationData":[TD([[subQ2,-1.0]])],"derivedFrom":subQ1}),1.0]])]});}
            var Q9;
            {var subQ5=sQuery(id+"F13.wireOp",EDGE,"E17.top");Q9=makeQuery(id+"F13.imprint","IMPRINT",FACE,{"disambiguationData":[TD([[makeQuery(id+"F13.imprint","IMPRINT",EDGE,{"derivedFrom":subQ5}),1.0]])]});}
            var Q10;
            {var subQ0=sQuery(id+"F13.wireOp",EDGE,"E16.bottom");var subQ1=sQuery(id+"F13.wireOp",EDGE,"E15.left");var subQ2=makeQuery(id+"F13.imprint","INTERSECT",VERTEX,{"derivedFrom":[subQ1,subQ0]});Q10=makeQuery(id+"F13.imprint","IMPRINT",FACE,{"disambiguationData":[TD([[makeQuery(id+"F13.imprint","IMPRINT",EDGE,{"disambiguationData":[TD([[subQ2,-1.0]])],"derivedFrom":subQ1}),1.0]])]});}
            var Q11;
            {var subQ5=sQuery(id+"F13.wireOp",EDGE,"E16.left");Q11=makeQuery(id+"F13.imprint","IMPRINT",FACE,{"disambiguationData":[TD([[makeQuery(id+"F13.imprint","IMPRINT",EDGE,{"derivedFrom":subQ5}),1.0]])]});}
            extrude(context, id + "F14", {"entities" : qUnion([Q0, Q1, Q2, Q3, Q4, Q5, Q6, Q7, Q8, Q9, Q10, Q11]), "depth" : 7.62 * mm});
        }
        {
            var Q0;
            {var subQ5=sQuery(id+"F13.wireOp",EDGE,"E16.left");Q0=makeQuery(id+"F13.imprint","IMPRINT",FACE,{"disambiguationData":[TD([[makeQuery(id+"F13.imprint","IMPRINT",EDGE,{"derivedFrom":subQ5}),1.0]])]});}
            var Q1;
            {var subQ0=sQuery(id+"F13.wireOp",EDGE,"E16.bottom");var subQ1=sQuery(id+"F13.wireOp",EDGE,"E15.left");var subQ2=makeQuery(id+"F13.imprint","INTERSECT",VERTEX,{"derivedFrom":[subQ1,subQ0]});Q1=makeQuery(id+"F13.imprint","IMPRINT",FACE,{"disambiguationData":[TD([[makeQuery(id+"F13.imprint","IMPRINT",EDGE,{"disambiguationData":[TD([[subQ2,-1.0]])],"derivedFrom":subQ1}),1.0]])]});}
            var Q2;
            {var subQ5=sQuery(id+"F13.wireOp",EDGE,"E17.bottom");Q2=makeQuery(id+"F13.imprint","IMPRINT",FACE,{"disambiguationData":[TD([[makeQuery(id+"F13.imprint","IMPRINT",EDGE,{"derivedFrom":subQ5}),-1.0]])]});}
            var Q3;
            {var subQ0=sQuery(id+"F13.wireOp",EDGE,"E16.bottom");var subQ1=sQuery(id+"F13.wireOp",EDGE,"E15.right");var subQ2=makeQuery(id+"F13.imprint","INTERSECT",VERTEX,{"derivedFrom":[subQ1,subQ0]});Q3=makeQuery(id+"F13.imprint","IMPRINT",FACE,{"disambiguationData":[TD([[makeQuery(id+"F13.imprint","IMPRINT",EDGE,{"disambiguationData":[TD([[subQ2,-1.0]])],"derivedFrom":subQ1}),-1.0]])]});}
            var Q4;
            {var subQ5=sQuery(id+"F13.wireOp",EDGE,"E16.right");Q4=makeQuery(id+"F13.imprint","IMPRINT",FACE,{"disambiguationData":[TD([[makeQuery(id+"F13.imprint","IMPRINT",EDGE,{"derivedFrom":subQ5}),-1.0]])]});}
            var Q5;
            {var subQ0=sQuery(id+"F13.wireOp",EDGE,"E17.left");var subQ1=sQuery(id+"F13.wireOp",EDGE,"E12.top");var subQ2=makeQuery(id+"F13.imprint","INTERSECT",VERTEX,{"derivedFrom":[subQ1,subQ0]});Q5=makeQuery(id+"F13.imprint","IMPRINT",FACE,{"disambiguationData":[TD([[makeQuery(id+"F13.imprint","IMPRINT",EDGE,{"disambiguationData":[TD([[subQ2,-1.0]])],"derivedFrom":subQ1}),1.0]])]});}
            var Q6;
            {var subQ5=sQuery(id+"F13.wireOp",EDGE,"E17.top");Q6=makeQuery(id+"F13.imprint","IMPRINT",FACE,{"disambiguationData":[TD([[makeQuery(id+"F13.imprint","IMPRINT",EDGE,{"derivedFrom":subQ5}),1.0]])]});}
            extrude(context, id + "F15", {"entities" : qUnion([Q0, Q1, Q2, Q3, Q4, Q5, Q6]), "depth" : 15.24 * mm, "hasSecondDirection" : true, "secondDirectionOppositeDirection" : false, "secondDirectionDepth" : 7.62 * mm});
        }
        {
            var Q0;
            Q0=makeQuery(id+"F0.imprint","IMPRINT",FACE,{"disambiguationData":[TD([[makeQuery(id+"F0.imprint","IMPRINT",EDGE,{"derivedFrom":sQuery(id+"F0.wireOp",EDGE,"E9.bottom")}),-1.0]])]});
            extrude(context, id + "F16", {"entities" : qUnion([Q0]), "depth" : 15.24 * mm, "hasSecondDirection" : true, "secondDirectionOppositeDirection" : false, "secondDirectionDepth" : 7.62 * mm});
        }
    });
